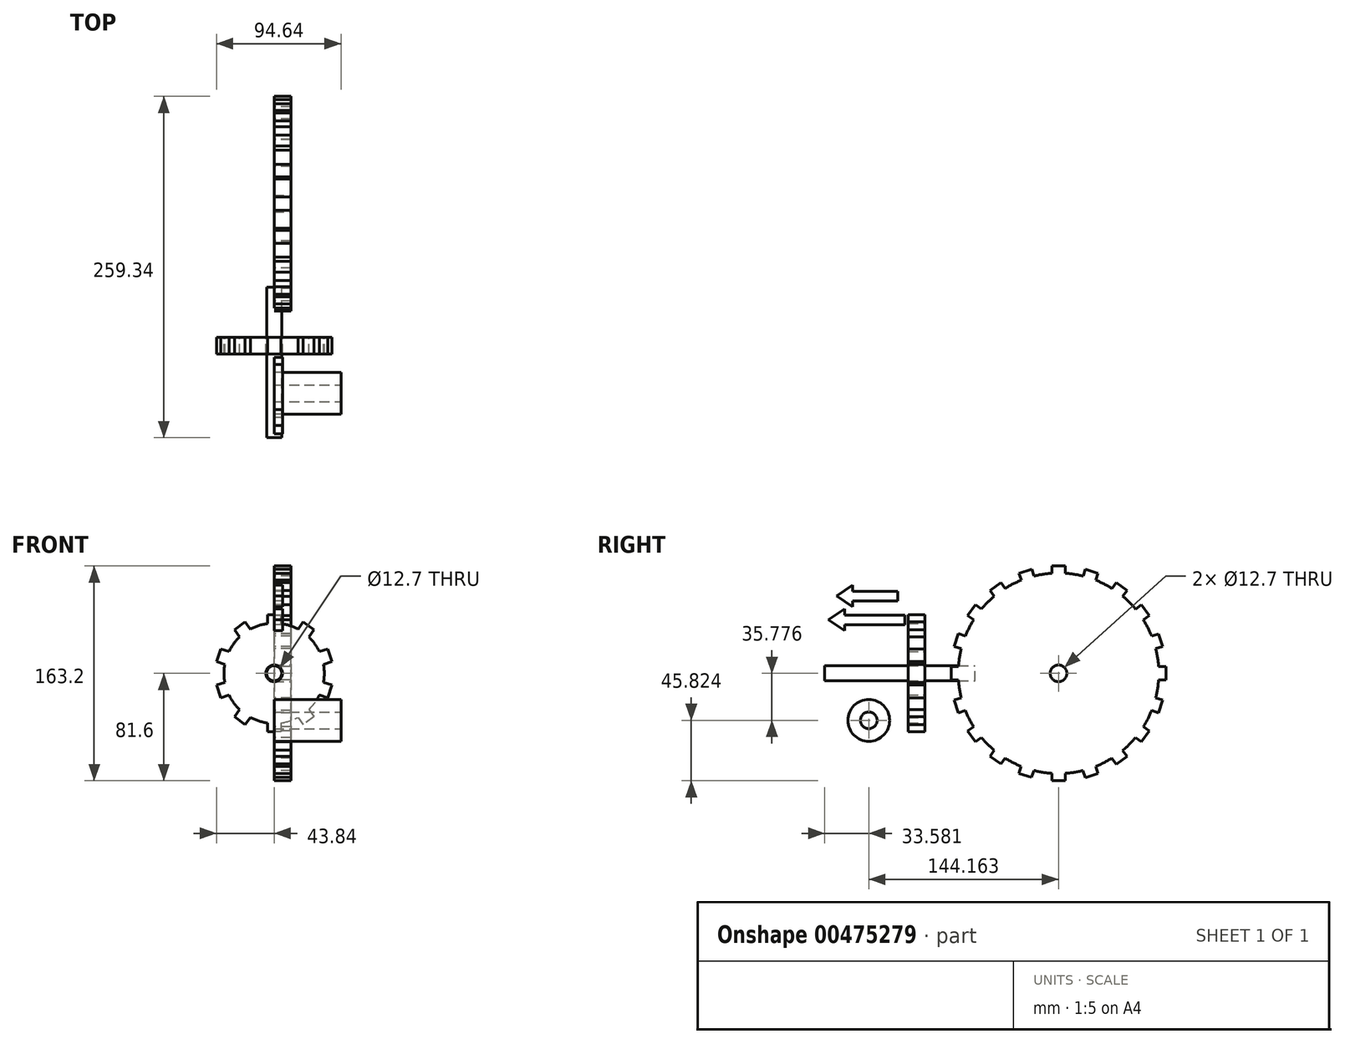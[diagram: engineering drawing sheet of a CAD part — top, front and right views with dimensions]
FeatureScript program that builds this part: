
annotation { "Feature Type Name" : "Feature", "Feature Type Description" : "" }
export const myFeature = defineFeature(function(context is Context, id is Id, definition is map)
    precondition{}
    {
        {
            var Q0;
            Q0=qCreatedBy(makeId("Front.planeOp"),FACE);
            var sketch = newSketch(context, id + "F0", { "sketchPlane" : qUnion([Q0])});
            skCircle(sketch, "E0", {"center": v(0, 0) * mm, "radius": 38.1 * mm});
            skSolve(sketch);
        }
        {
            var Q0;
            Q0=makeQuery(id+"F0.imprint","IMPRINT",FACE,{"disambiguationData":[TD([[makeQuery(id+"F0.imprint","IMPRINT",EDGE,{"derivedFrom":sQuery(id+"F0.wireOp",EDGE,"E0")}),1.0]])]});
            var sketch = newSketch(context, id + "F1", { "sketchPlane" : qUnion([Q0])});
            skLineSegment(sketch, "E1.bottom", {"start": v(-5.08, 36.83) * mm, "end": v(5.08, 36.83) * mm});
            skLineSegment(sketch, "E1.top", {"start": v(-5.08, 44.45) * mm, "end": v(5.08, 44.45) * mm});
            skLineSegment(sketch, "E1.left", {"start": v(-5.08, 36.83) * mm, "end": v(-5.08, 44.45) * mm});
            skLineSegment(sketch, "E1.right", {"start": v(5.08, 36.83) * mm, "end": v(5.08, 44.45) * mm});
            skSolve(sketch);
        }
        {
            var Q0;
            Q0=qSketchRegion(id+"F0",true);
            var Q1;
            {var subQ0=sQuery(id+"F1.wireOp",EDGE,"E1.top");Q1=makeQuery(id+"F1.imprint","IMPRINT",FACE,{"disambiguationData":[TD([[makeQuery(id+"F1.imprint","IMPRINT",EDGE,{"derivedFrom":subQ0}),-1.0]])]});}
            extrude(context, id + "F2", {"entities" : qUnion([Q0, Q1]), "depth" : 12.7 * mm});
        }
        {
            var Q0;
            Q0=makeQuery(id+"F2.opExtrude","SWEPT_BODY",BODY,{"disambiguationData":[OSD([sQuery(id+"F0.wireOp",EDGE,"E0"),sQuery(id+"F1.wireOp",EDGE,"E1.top"),sQuery(id+"F1.wireOp",EDGE,"E1.left"),sQuery(id+"F1.wireOp",EDGE,"E1.right")])]});
            var Q1;
            Q1=sQuery(id+"F0.wireOp",EDGE,"E0");
            circularPattern(context, id + "F3", {"entities" : qUnion([Q0]), "axis" : qUnion([Q1]), "angle" : 360 * degree, "instanceCount" : 10, "equalSpace" : true});
        }
        {
            var Q0;
            Q0=sQuery(id+"F0.wireOp",VERTEX,"E0.center");
            var Q1;
            Q1=makeQuery(id+"F2.opExtrude","SWEPT_BODY",BODY,{"disambiguationData":[OSD([sQuery(id+"F0.wireOp",EDGE,"E0")])]});
            hole(context, id + "F4", {"style" : HoleStyle.SIMPLE, "endStyle" : HoleEndStyle.THROUGH, "oppositeDirection" : true, "holeDiameter" : 12.7 * mm, "tappedDepth" : 12.7 * mm, "tapClearance" : 3, "locations" : qUnion([Q0]), "scope" : qUnion([Q1])});
        }
        {
            var Q0;
            Q0=makeQuery(id+"F2.opExtrude","SWEPT_BODY",BODY,{"disambiguationData":[OSD([sQuery(id+"F0.wireOp",EDGE,"E0"),sQuery(id+"F1.wireOp",EDGE,"E1.top"),sQuery(id+"F1.wireOp",EDGE,"E1.left"),sQuery(id+"F1.wireOp",EDGE,"E1.right")])]});
            var Q1;
            Q1=makeQuery(id+"F3.opPattern","COPY",BODY,{"derivedFrom":makeQuery(id+"F2.opExtrude","SWEPT_BODY",BODY,{"disambiguationData":[OSD([sQuery(id+"F0.wireOp",EDGE,"E0"),sQuery(id+"F1.wireOp",EDGE,"E1.top"),sQuery(id+"F1.wireOp",EDGE,"E1.left"),sQuery(id+"F1.wireOp",EDGE,"E1.right")])]}),"instanceName":"2"});
            var Q2;
            Q2=makeQuery(id+"F3.opPattern","COPY",BODY,{"derivedFrom":makeQuery(id+"F2.opExtrude","SWEPT_BODY",BODY,{"disambiguationData":[OSD([sQuery(id+"F0.wireOp",EDGE,"E0"),sQuery(id+"F1.wireOp",EDGE,"E1.top"),sQuery(id+"F1.wireOp",EDGE,"E1.left"),sQuery(id+"F1.wireOp",EDGE,"E1.right")])]}),"instanceName":"1"});
            var Q3;
            Q3=makeQuery(id+"F3.opPattern","COPY",BODY,{"derivedFrom":makeQuery(id+"F2.opExtrude","SWEPT_BODY",BODY,{"disambiguationData":[OSD([sQuery(id+"F0.wireOp",EDGE,"E0"),sQuery(id+"F1.wireOp",EDGE,"E1.top"),sQuery(id+"F1.wireOp",EDGE,"E1.left"),sQuery(id+"F1.wireOp",EDGE,"E1.right")])]}),"instanceName":"3"});
            var Q4;
            Q4=makeQuery(id+"F3.opPattern","COPY",BODY,{"derivedFrom":makeQuery(id+"F2.opExtrude","SWEPT_BODY",BODY,{"disambiguationData":[OSD([sQuery(id+"F0.wireOp",EDGE,"E0"),sQuery(id+"F1.wireOp",EDGE,"E1.top"),sQuery(id+"F1.wireOp",EDGE,"E1.left"),sQuery(id+"F1.wireOp",EDGE,"E1.right")])]}),"instanceName":"4"});
            var Q5;
            Q5=makeQuery(id+"F3.opPattern","COPY",BODY,{"derivedFrom":makeQuery(id+"F2.opExtrude","SWEPT_BODY",BODY,{"disambiguationData":[OSD([sQuery(id+"F0.wireOp",EDGE,"E0"),sQuery(id+"F1.wireOp",EDGE,"E1.top"),sQuery(id+"F1.wireOp",EDGE,"E1.left"),sQuery(id+"F1.wireOp",EDGE,"E1.right")])]}),"instanceName":"5"});
            var Q6;
            Q6=makeQuery(id+"F3.opPattern","COPY",BODY,{"derivedFrom":makeQuery(id+"F2.opExtrude","SWEPT_BODY",BODY,{"disambiguationData":[OSD([sQuery(id+"F0.wireOp",EDGE,"E0"),sQuery(id+"F1.wireOp",EDGE,"E1.top"),sQuery(id+"F1.wireOp",EDGE,"E1.left"),sQuery(id+"F1.wireOp",EDGE,"E1.right")])]}),"instanceName":"6"});
            var Q7;
            Q7=makeQuery(id+"F3.opPattern","COPY",BODY,{"derivedFrom":makeQuery(id+"F2.opExtrude","SWEPT_BODY",BODY,{"disambiguationData":[OSD([sQuery(id+"F0.wireOp",EDGE,"E0"),sQuery(id+"F1.wireOp",EDGE,"E1.top"),sQuery(id+"F1.wireOp",EDGE,"E1.left"),sQuery(id+"F1.wireOp",EDGE,"E1.right")])]}),"instanceName":"7"});
            var Q8;
            Q8=makeQuery(id+"F3.opPattern","COPY",BODY,{"derivedFrom":makeQuery(id+"F2.opExtrude","SWEPT_BODY",BODY,{"disambiguationData":[OSD([sQuery(id+"F0.wireOp",EDGE,"E0"),sQuery(id+"F1.wireOp",EDGE,"E1.top"),sQuery(id+"F1.wireOp",EDGE,"E1.left"),sQuery(id+"F1.wireOp",EDGE,"E1.right")])]}),"instanceName":"8"});
            var Q9;
            Q9=makeQuery(id+"F3.opPattern","COPY",BODY,{"derivedFrom":makeQuery(id+"F2.opExtrude","SWEPT_BODY",BODY,{"disambiguationData":[OSD([sQuery(id+"F0.wireOp",EDGE,"E0"),sQuery(id+"F1.wireOp",EDGE,"E1.top"),sQuery(id+"F1.wireOp",EDGE,"E1.left"),sQuery(id+"F1.wireOp",EDGE,"E1.right")])]}),"instanceName":"9"});
            var Q10;
            Q10=makeQuery(id+"F2.opExtrude","SWEPT_BODY",BODY,{"disambiguationData":[OSD([sQuery(id+"F0.wireOp",EDGE,"E0")])]});
            booleanBodies(context, id + "F5", {"operationType" : BooleanOperationType.UNION, "tools" : qUnion([Q0, Q1, Q2, Q3, Q4, Q5, Q6, Q7, Q8, Q9, Q10])});
        }
        {
            var Q0;
            Q0=qCreatedBy(makeId("Right.planeOp"),FACE);
            var sketch = newSketch(context, id + "F6", { "sketchPlane" : qUnion([Q0])});
            skCircle(sketch, "E2", {"center": v(101.54, 0) * mm, "radius": 76.2 * mm});
            skSolve(sketch);
        }
        {
            var Q0;
            Q0=makeQuery(id+"F6.imprint","IMPRINT",FACE,{"disambiguationData":[TD([[makeQuery(id+"F6.imprint","IMPRINT",EDGE,{"derivedFrom":sQuery(id+"F6.wireOp",EDGE,"E2")}),1.0]])]});
            var sketch = newSketch(context, id + "F7", { "sketchPlane" : qUnion([Q0])});
            skLineSegment(sketch, "E3.bottom", {"start": v(96.49, 73.98) * mm, "end": v(106.65, 73.98) * mm});
            skLineSegment(sketch, "E3.top", {"start": v(96.49, 81.6) * mm, "end": v(106.65, 81.6) * mm});
            skLineSegment(sketch, "E3.left", {"start": v(96.49, 73.98) * mm, "end": v(96.49, 81.6) * mm});
            skLineSegment(sketch, "E3.right", {"start": v(106.65, 73.98) * mm, "end": v(106.65, 81.6) * mm});
            skSolve(sketch);
        }
        {
            var Q0;
            Q0=makeQuery(id+"F6.imprint","IMPRINT",FACE,{"disambiguationData":[TD([[makeQuery(id+"F6.imprint","IMPRINT",EDGE,{"derivedFrom":sQuery(id+"F6.wireOp",EDGE,"E2")}),1.0]])]});
            var Q1;
            Q1=makeQuery(id+"F7.imprint","IMPRINT",FACE,{"disambiguationData":[TD([[makeQuery(id+"F7.imprint","IMPRINT",EDGE,{"derivedFrom":sQuery(id+"F7.wireOp",EDGE,"E3.top")}),-1.0]])]});
            extrude(context, id + "F8", {"entities" : qUnion([Q0, Q1]), "depth" : 12.7 * mm});
        }
        {
            var Q0;
            Q0=makeQuery(id+"F8.opExtrude","SWEPT_BODY",BODY,{"disambiguationData":[OSD([sQuery(id+"F6.wireOp",EDGE,"E2"),sQuery(id+"F7.wireOp",EDGE,"E3.bottom"),sQuery(id+"F7.wireOp",EDGE,"E3.top"),sQuery(id+"F7.wireOp",EDGE,"E3.left"),sQuery(id+"F7.wireOp",EDGE,"E3.right")])]});
            var Q1;
            {var subQ0=sQuery(id+"F6.wireOp",EDGE,"E2");Q1=makeQuery(id+"F8.opExtrude","CAP_EDGE",EDGE,{"disambiguationData":[OSD([subQ0]),TDD([makeQuery(id+"F6.imprint","IMPRINT",EDGE,{"derivedFrom":subQ0})])],"isStart":false});}
            circularPattern(context, id + "F9", {"entities" : qUnion([Q0]), "axis" : qUnion([Q1]), "angle" : 360 * degree, "instanceCount" : 20, "equalSpace" : true});
        }
        {
            var Q0;
            Q0=makeQuery(id+"F9.opPattern","COPY",BODY,{"derivedFrom":makeQuery(id+"F8.opExtrude","SWEPT_BODY",BODY,{"disambiguationData":[OSD([sQuery(id+"F6.wireOp",EDGE,"E2"),sQuery(id+"F7.wireOp",EDGE,"E3.bottom"),sQuery(id+"F7.wireOp",EDGE,"E3.top"),sQuery(id+"F7.wireOp",EDGE,"E3.left"),sQuery(id+"F7.wireOp",EDGE,"E3.right")])]}),"instanceName":"1"});
            var Q1;
            Q1=makeQuery(id+"F9.opPattern","COPY",BODY,{"derivedFrom":makeQuery(id+"F8.opExtrude","SWEPT_BODY",BODY,{"disambiguationData":[OSD([sQuery(id+"F6.wireOp",EDGE,"E2"),sQuery(id+"F7.wireOp",EDGE,"E3.bottom"),sQuery(id+"F7.wireOp",EDGE,"E3.top"),sQuery(id+"F7.wireOp",EDGE,"E3.left"),sQuery(id+"F7.wireOp",EDGE,"E3.right")])]}),"instanceName":"2"});
            var Q2;
            Q2=makeQuery(id+"F8.opExtrude","SWEPT_BODY",BODY,{"disambiguationData":[OSD([sQuery(id+"F6.wireOp",EDGE,"E2")])]});
            var Q3;
            Q3=makeQuery(id+"F8.opExtrude","SWEPT_BODY",BODY,{"disambiguationData":[OSD([sQuery(id+"F6.wireOp",EDGE,"E2"),sQuery(id+"F7.wireOp",EDGE,"E3.bottom"),sQuery(id+"F7.wireOp",EDGE,"E3.top"),sQuery(id+"F7.wireOp",EDGE,"E3.left"),sQuery(id+"F7.wireOp",EDGE,"E3.right")])]});
            var Q4;
            Q4=makeQuery(id+"F9.opPattern","COPY",BODY,{"derivedFrom":makeQuery(id+"F8.opExtrude","SWEPT_BODY",BODY,{"disambiguationData":[OSD([sQuery(id+"F6.wireOp",EDGE,"E2"),sQuery(id+"F7.wireOp",EDGE,"E3.bottom"),sQuery(id+"F7.wireOp",EDGE,"E3.top"),sQuery(id+"F7.wireOp",EDGE,"E3.left"),sQuery(id+"F7.wireOp",EDGE,"E3.right")])]}),"instanceName":"9"});
            var Q5;
            Q5=makeQuery(id+"F9.opPattern","COPY",BODY,{"derivedFrom":makeQuery(id+"F8.opExtrude","SWEPT_BODY",BODY,{"disambiguationData":[OSD([sQuery(id+"F6.wireOp",EDGE,"E2"),sQuery(id+"F7.wireOp",EDGE,"E3.bottom"),sQuery(id+"F7.wireOp",EDGE,"E3.top"),sQuery(id+"F7.wireOp",EDGE,"E3.left"),sQuery(id+"F7.wireOp",EDGE,"E3.right")])]}),"instanceName":"8"});
            var Q6;
            Q6=makeQuery(id+"F9.opPattern","COPY",BODY,{"derivedFrom":makeQuery(id+"F8.opExtrude","SWEPT_BODY",BODY,{"disambiguationData":[OSD([sQuery(id+"F6.wireOp",EDGE,"E2"),sQuery(id+"F7.wireOp",EDGE,"E3.bottom"),sQuery(id+"F7.wireOp",EDGE,"E3.top"),sQuery(id+"F7.wireOp",EDGE,"E3.left"),sQuery(id+"F7.wireOp",EDGE,"E3.right")])]}),"instanceName":"7"});
            var Q7;
            Q7=makeQuery(id+"F9.opPattern","COPY",BODY,{"derivedFrom":makeQuery(id+"F8.opExtrude","SWEPT_BODY",BODY,{"disambiguationData":[OSD([sQuery(id+"F6.wireOp",EDGE,"E2"),sQuery(id+"F7.wireOp",EDGE,"E3.bottom"),sQuery(id+"F7.wireOp",EDGE,"E3.top"),sQuery(id+"F7.wireOp",EDGE,"E3.left"),sQuery(id+"F7.wireOp",EDGE,"E3.right")])]}),"instanceName":"6"});
            var Q8;
            Q8=makeQuery(id+"F9.opPattern","COPY",BODY,{"derivedFrom":makeQuery(id+"F8.opExtrude","SWEPT_BODY",BODY,{"disambiguationData":[OSD([sQuery(id+"F6.wireOp",EDGE,"E2"),sQuery(id+"F7.wireOp",EDGE,"E3.bottom"),sQuery(id+"F7.wireOp",EDGE,"E3.top"),sQuery(id+"F7.wireOp",EDGE,"E3.left"),sQuery(id+"F7.wireOp",EDGE,"E3.right")])]}),"instanceName":"5"});
            var Q9;
            Q9=makeQuery(id+"F9.opPattern","COPY",BODY,{"derivedFrom":makeQuery(id+"F8.opExtrude","SWEPT_BODY",BODY,{"disambiguationData":[OSD([sQuery(id+"F6.wireOp",EDGE,"E2"),sQuery(id+"F7.wireOp",EDGE,"E3.bottom"),sQuery(id+"F7.wireOp",EDGE,"E3.top"),sQuery(id+"F7.wireOp",EDGE,"E3.left"),sQuery(id+"F7.wireOp",EDGE,"E3.right")])]}),"instanceName":"4"});
            var Q10;
            Q10=makeQuery(id+"F9.opPattern","COPY",BODY,{"derivedFrom":makeQuery(id+"F8.opExtrude","SWEPT_BODY",BODY,{"disambiguationData":[OSD([sQuery(id+"F6.wireOp",EDGE,"E2"),sQuery(id+"F7.wireOp",EDGE,"E3.bottom"),sQuery(id+"F7.wireOp",EDGE,"E3.top"),sQuery(id+"F7.wireOp",EDGE,"E3.left"),sQuery(id+"F7.wireOp",EDGE,"E3.right")])]}),"instanceName":"3"});
            var Q11;
            Q11=makeQuery(id+"F9.opPattern","COPY",BODY,{"derivedFrom":makeQuery(id+"F8.opExtrude","SWEPT_BODY",BODY,{"disambiguationData":[OSD([sQuery(id+"F6.wireOp",EDGE,"E2"),sQuery(id+"F7.wireOp",EDGE,"E3.top"),sQuery(id+"F7.wireOp",EDGE,"E3.left"),sQuery(id+"F7.wireOp",EDGE,"E3.right")])]}),"instanceName":"19"});
            var Q12;
            Q12=makeQuery(id+"F9.opPattern","COPY",BODY,{"derivedFrom":makeQuery(id+"F8.opExtrude","SWEPT_BODY",BODY,{"disambiguationData":[OSD([sQuery(id+"F6.wireOp",EDGE,"E2"),sQuery(id+"F7.wireOp",EDGE,"E3.top"),sQuery(id+"F7.wireOp",EDGE,"E3.left"),sQuery(id+"F7.wireOp",EDGE,"E3.right")])]}),"instanceName":"18"});
            var Q13;
            Q13=makeQuery(id+"F9.opPattern","COPY",BODY,{"derivedFrom":makeQuery(id+"F8.opExtrude","SWEPT_BODY",BODY,{"disambiguationData":[OSD([sQuery(id+"F6.wireOp",EDGE,"E2"),sQuery(id+"F7.wireOp",EDGE,"E3.top"),sQuery(id+"F7.wireOp",EDGE,"E3.left"),sQuery(id+"F7.wireOp",EDGE,"E3.right")])]}),"instanceName":"17"});
            var Q14;
            Q14=makeQuery(id+"F9.opPattern","COPY",BODY,{"derivedFrom":makeQuery(id+"F8.opExtrude","SWEPT_BODY",BODY,{"disambiguationData":[OSD([sQuery(id+"F6.wireOp",EDGE,"E2"),sQuery(id+"F7.wireOp",EDGE,"E3.top"),sQuery(id+"F7.wireOp",EDGE,"E3.left"),sQuery(id+"F7.wireOp",EDGE,"E3.right")])]}),"instanceName":"16"});
            var Q15;
            Q15=makeQuery(id+"F9.opPattern","COPY",BODY,{"derivedFrom":makeQuery(id+"F8.opExtrude","SWEPT_BODY",BODY,{"disambiguationData":[OSD([sQuery(id+"F6.wireOp",EDGE,"E2"),sQuery(id+"F7.wireOp",EDGE,"E3.top"),sQuery(id+"F7.wireOp",EDGE,"E3.left"),sQuery(id+"F7.wireOp",EDGE,"E3.right")])]}),"instanceName":"15"});
            var Q16;
            Q16=makeQuery(id+"F9.opPattern","COPY",BODY,{"derivedFrom":makeQuery(id+"F8.opExtrude","SWEPT_BODY",BODY,{"disambiguationData":[OSD([sQuery(id+"F6.wireOp",EDGE,"E2"),sQuery(id+"F7.wireOp",EDGE,"E3.top"),sQuery(id+"F7.wireOp",EDGE,"E3.left"),sQuery(id+"F7.wireOp",EDGE,"E3.right")])]}),"instanceName":"14"});
            var Q17;
            Q17=makeQuery(id+"F9.opPattern","COPY",BODY,{"derivedFrom":makeQuery(id+"F8.opExtrude","SWEPT_BODY",BODY,{"disambiguationData":[OSD([sQuery(id+"F6.wireOp",EDGE,"E2"),sQuery(id+"F7.wireOp",EDGE,"E3.top"),sQuery(id+"F7.wireOp",EDGE,"E3.left"),sQuery(id+"F7.wireOp",EDGE,"E3.right")])]}),"instanceName":"13"});
            var Q18;
            Q18=makeQuery(id+"F9.opPattern","COPY",BODY,{"derivedFrom":makeQuery(id+"F8.opExtrude","SWEPT_BODY",BODY,{"disambiguationData":[OSD([sQuery(id+"F6.wireOp",EDGE,"E2"),sQuery(id+"F7.wireOp",EDGE,"E3.top"),sQuery(id+"F7.wireOp",EDGE,"E3.left"),sQuery(id+"F7.wireOp",EDGE,"E3.right")])]}),"instanceName":"12"});
            var Q19;
            Q19=makeQuery(id+"F9.opPattern","COPY",BODY,{"derivedFrom":makeQuery(id+"F8.opExtrude","SWEPT_BODY",BODY,{"disambiguationData":[OSD([sQuery(id+"F6.wireOp",EDGE,"E2"),sQuery(id+"F7.wireOp",EDGE,"E3.top"),sQuery(id+"F7.wireOp",EDGE,"E3.left"),sQuery(id+"F7.wireOp",EDGE,"E3.right")])]}),"instanceName":"11"});
            var Q20;
            Q20=makeQuery(id+"F9.opPattern","COPY",BODY,{"derivedFrom":makeQuery(id+"F8.opExtrude","SWEPT_BODY",BODY,{"disambiguationData":[OSD([sQuery(id+"F6.wireOp",EDGE,"E2"),sQuery(id+"F7.wireOp",EDGE,"E3.top"),sQuery(id+"F7.wireOp",EDGE,"E3.left"),sQuery(id+"F7.wireOp",EDGE,"E3.right")])]}),"instanceName":"10"});
            booleanBodies(context, id + "F10", {"operationType" : BooleanOperationType.UNION, "tools" : qUnion([Q0, Q1, Q2, Q3, Q4, Q5, Q6, Q7, Q8, Q9, Q10, Q11, Q12, Q13, Q14, Q15, Q16, Q17, Q18, Q19, Q20])});
        }
        {
            var Q0;
            {var subQ0=sQuery(id+"F6.wireOp",EDGE,"E2");var subQ1=makeQuery(id+"F8.opExtrude","CAP_FACE",FACE,{"disambiguationData":[OSD([subQ0,sQuery(id+"F7.wireOp",EDGE,"E3.top"),sQuery(id+"F7.wireOp",EDGE,"E3.left"),sQuery(id+"F7.wireOp",EDGE,"E3.right")])],"isStart":false});Q0=makeQuery(id+"F10.opBoolean","MERGE",FACE,{"derivedFrom":[makeQuery(id+"F8.opExtrude","CAP_FACE",FACE,{"disambiguationData":[OSD([subQ0])],"isStart":false}),subQ1,makeQuery(id+"F9.opPattern","COPY",FACE,{"derivedFrom":subQ1,"instanceName":"1"}),makeQuery(id+"F9.opPattern","COPY",FACE,{"derivedFrom":subQ1,"instanceName":"2"}),makeQuery(id+"F9.opPattern","COPY",FACE,{"derivedFrom":subQ1,"instanceName":"3"}),makeQuery(id+"F9.opPattern","COPY",FACE,{"derivedFrom":subQ1,"instanceName":"4"}),makeQuery(id+"F9.opPattern","COPY",FACE,{"derivedFrom":subQ1,"instanceName":"5"}),makeQuery(id+"F9.opPattern","COPY",FACE,{"derivedFrom":subQ1,"instanceName":"6"}),makeQuery(id+"F9.opPattern","COPY",FACE,{"derivedFrom":subQ1,"instanceName":"7"}),makeQuery(id+"F9.opPattern","COPY",FACE,{"derivedFrom":subQ1,"instanceName":"8"}),makeQuery(id+"F9.opPattern","COPY",FACE,{"derivedFrom":subQ1,"instanceName":"9"})]});}
            var sketch = newSketch(context, id + "F11", { "sketchPlane" : qUnion([Q0])});
            skPoint(sketch, "E4", {"position": v(101.54, 0) * mm});
            skSolve(sketch);
        }
        {
            var Q0;
            Q0=sQuery(id+"F11.wireOp",VERTEX,"E4");
            var Q1;
            Q1=makeQuery(id+"F9.opPattern","COPY",BODY,{"derivedFrom":makeQuery(id+"F8.opExtrude","SWEPT_BODY",BODY,{"disambiguationData":[OSD([sQuery(id+"F6.wireOp",EDGE,"E2"),sQuery(id+"F7.wireOp",EDGE,"E3.top"),sQuery(id+"F7.wireOp",EDGE,"E3.left"),sQuery(id+"F7.wireOp",EDGE,"E3.right")])]}),"instanceName":"1"});
            hole(context, id + "F12", {"style" : HoleStyle.SIMPLE, "endStyle" : HoleEndStyle.THROUGH, "holeDiameter" : 12.7 * mm, "tappedDepth" : 12.7 * mm, "tapClearance" : 3, "locations" : qUnion([Q0]), "scope" : qUnion([Q1])});
        }
        {
            var Q0;
            {var subQ0=sQuery(id+"F0.wireOp",EDGE,"E0");var subQ1=makeQuery(id+"F2.opExtrude","CAP_FACE",FACE,{"disambiguationData":[OSD([subQ0,sQuery(id+"F1.wireOp",EDGE,"E1.top"),sQuery(id+"F1.wireOp",EDGE,"E1.left"),sQuery(id+"F1.wireOp",EDGE,"E1.right")])],"isStart":false});Q0=makeQuery(id+"F5.opBoolean","MERGE",FACE,{"derivedFrom":[subQ1,makeQuery(id+"F3.opPattern","COPY",FACE,{"derivedFrom":subQ1,"instanceName":"1"}),makeQuery(id+"F3.opPattern","COPY",FACE,{"derivedFrom":subQ1,"instanceName":"2"}),makeQuery(id+"F3.opPattern","COPY",FACE,{"derivedFrom":subQ1,"instanceName":"3"}),makeQuery(id+"F3.opPattern","COPY",FACE,{"derivedFrom":subQ1,"instanceName":"4"}),makeQuery(id+"F3.opPattern","COPY",FACE,{"derivedFrom":subQ1,"instanceName":"5"}),makeQuery(id+"F3.opPattern","COPY",FACE,{"derivedFrom":subQ1,"instanceName":"6"}),makeQuery(id+"F3.opPattern","COPY",FACE,{"derivedFrom":subQ1,"instanceName":"7"}),makeQuery(id+"F3.opPattern","COPY",FACE,{"derivedFrom":subQ1,"instanceName":"8"}),makeQuery(id+"F3.opPattern","COPY",FACE,{"derivedFrom":subQ1,"instanceName":"9"}),makeQuery(id+"F2.opExtrude","CAP_FACE",FACE,{"disambiguationData":[OSD([subQ0])],"isStart":false})]});}
            var sketch = newSketch(context, id + "F13", { "sketchPlane" : qUnion([Q0])});
            skCircle(sketch, "E5", {"center": v(0, 0) * mm, "radius": 5.72 * mm});
            skSolve(sketch);
        }
        {
            var Q0;
            Q0 = qSketchRegion(id + "F13", true);
            extrude(context, id + "F14", {"entities" : qUnion([Q0]), "depth" : 63.5 * mm, "hasSecondDirection" : true, "secondDirectionOppositeDirection" : true, "secondDirectionDepth" : 50.8 * mm});
        }
        {
            var Q0;
            Q0=qCreatedBy(makeId("Right.planeOp"),FACE);
            var sketch = newSketch(context, id + "F15", { "sketchPlane" : qUnion([Q0])});
            skLineSegment(sketch, "E6.bottom", {"start": v(-20.69, 62.38) * mm, "end": v(-54.92, 62.38) * mm});
            skLineSegment(sketch, "E6.top", {"start": v(-20.69, 54.95) * mm, "end": v(-54.92, 54.95) * mm});
            skLineSegment(sketch, "E6.left", {"start": v(-20.69, 62.38) * mm, "end": v(-20.69, 54.95) * mm});
            skLineSegment(sketch, "E6.right", {"start": v(-54.92, 62.38) * mm, "end": v(-54.92, 54.95) * mm});
            skLineSegment(sketch, "E7", {"start": v(-54.92, 50.42) * mm, "end": v(-54.92, 66.92) * mm});
            skLineSegment(sketch, "E8", {"start": v(-54.92, 50.42) * mm, "end": v(-67.08, 58.66) * mm});
            skPoint(sketch, "E8.endSnap0", {"position": v(-54.92, 58.66) * mm});
            skLineSegment(sketch, "E9", {"start": v(-54.92, 66.92) * mm, "end": v(-67.08, 58.66) * mm});
            skSolve(sketch);
        }
        {
            var Q0;
            {var subQ0=sQuery(id+"F15.wireOp",EDGE,"E6.bottom");Q0=makeQuery(id+"F15.imprint","IMPRINT",FACE,{"disambiguationData":[TD([[makeQuery(id+"F15.imprint","IMPRINT",EDGE,{"derivedFrom":subQ0}),1.0]])]});}
            var Q1;
            {var subQ0=sQuery(id+"F15.wireOp",EDGE,"E8");Q1=makeQuery(id+"F15.imprint","IMPRINT",FACE,{"disambiguationData":[TD([[makeQuery(id+"F15.imprint","IMPRINT",EDGE,{"derivedFrom":subQ0}),-1.0]])]});}
            extrude(context, id + "F16", {"entities" : qUnion([Q0, Q1]), "depth" : 6.35 * mm});
        }
        {
            var Q0;
            Q0=qCreatedBy(makeId("Right.planeOp"),FACE);
            var sketch = newSketch(context, id + "F17", { "sketchPlane" : qUnion([Q0])});
            skCircle(sketch, "E10", {"center": v(-42.62, -35.78) * mm, "radius": 15.88 * mm});
            skSolve(sketch);
        }
        {
            var Q0;
            Q0=makeQuery(id+"F17.imprint","IMPRINT",FACE,{"disambiguationData":[TD([[makeQuery(id+"F17.imprint","IMPRINT",EDGE,{"derivedFrom":sQuery(id+"F17.wireOp",EDGE,"E10")}),1.0]])]});
            extrude(context, id + "F18", {"entities" : qUnion([Q0]), "depth" : 50.8 * mm});
        }
        {
            var Q0;
            Q0=makeQuery(id+"F18.opExtrude","CAP_FACE",FACE,{"disambiguationData":[OSD([sQuery(id+"F17.wireOp",EDGE,"E10")])],"isStart":false});
            var sketch = newSketch(context, id + "F19", { "sketchPlane" : qUnion([Q0])});
            skPoint(sketch, "E11", {"position": v(-42.62, -35.78) * mm});
            skSolve(sketch);
        }
        {
            var Q0;
            Q0=sQuery(id+"F19.wireOp",VERTEX,"E11");
            var Q1;
            Q1=makeQuery(id+"F18.opExtrude","SWEPT_BODY",BODY,{"disambiguationData":[OSD([sQuery(id+"F17.wireOp",EDGE,"E10")])]});
            hole(context, id + "F20", {"style" : HoleStyle.SIMPLE, "endStyle" : HoleEndStyle.THROUGH, "holeDiameter" : 12.7 * mm, "tappedDepth" : 12.7 * mm, "tapClearance" : 3, "locations" : qUnion([Q0]), "scope" : qUnion([Q1])});
        }
        {
            var Q0;
            Q0=qCreatedBy(makeId("Right.planeOp"),FACE);
            var sketch = newSketch(context, id + "F21", { "sketchPlane" : qUnion([Q0])});
            skLineSegment(sketch, "E12.bottom", {"start": v(-15.34, 44.3) * mm, "end": v(-61.06, 44.3) * mm});
            skLineSegment(sketch, "E12.top", {"start": v(-15.34, 36.94) * mm, "end": v(-61.06, 36.94) * mm});
            skLineSegment(sketch, "E12.left", {"start": v(-15.34, 44.3) * mm, "end": v(-15.34, 36.94) * mm});
            skLineSegment(sketch, "E12.right", {"start": v(-61.06, 44.3) * mm, "end": v(-61.06, 36.94) * mm});
            skLineSegment(sketch, "E13", {"start": v(-61.06, 32.4) * mm, "end": v(-61.06, 48.85) * mm});
            skLineSegment(sketch, "E14", {"start": v(-61.06, 48.85) * mm, "end": v(-73.22, 40.62) * mm});
            skPoint(sketch, "E14.endSnap0", {"position": v(-61.06, 40.62) * mm});
            skLineSegment(sketch, "E15", {"start": v(-73.22, 40.62) * mm, "end": v(-61.06, 32.4) * mm});
            skSolve(sketch);
        }
        {
            var Q0;
            Q0 = qSketchRegion(id + "F21", true);
            extrude(context, id + "F22", {"entities" : qUnion([Q0]), "depth" : 6.35 * mm});
        }
    });
